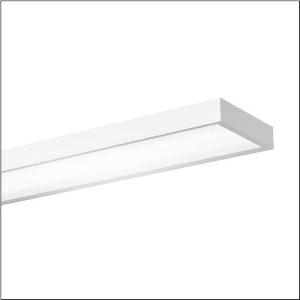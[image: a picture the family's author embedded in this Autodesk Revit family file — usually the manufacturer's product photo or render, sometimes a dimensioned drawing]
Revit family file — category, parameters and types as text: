
# Revit family: sport_31_51hs12dd4gca
name_source: partatom
category: Lighting Fixtures
units: mm (PartAtom-declared; Revit-internal decimal feet)

## family parameters
Cut with Voids When Loaded = No
Host = Face
Light Source = No
Part Type = Normal
Room Calculation Point = No
Round Connector Dimension = Use Diameter
Shared = No

## types (1)
- --- (1 x LED, 15290 lm, 113 W, 4000K)
    Apparent Load = 113 VA
    CIE Flux Codes = 65 89 97 100 100
    Color Rendering = 80
    Color Temperature = 4000K
    Default Elevation = 1800 mm
    Description = Sport 31, LED high bay luminaire, primary light control with reflector, of sheet steel, primary anti-glare with prismatic structure, of PC, primary optical cover: cover panel, of PC, light emission: direct distribution, primary light characteristic: symmetric, installation type: suspended mounting, recessed, surface-mounted, LED, rated luminous flux: 16.000lm, luminous efficacy: 137lm/W, light colour: 840, colour temperature: 4000K, control gear: ECG DALI, with terminal, 5-pole, max. 2.5mm², mains connection: 220..240V, AC/DC, 50/60Hz, rated input power: 117W, housing, of sheet steel, traffic white (RAL 9016), length: 1.540mm, width: 415mm, height: 95mm, protection rating (complete): IP20, protection rating (lamp compartment, on room side): IP50, insulation class (complete): insulation class I (protective earthing), certification: CE, ENEC, UKCA, ball protection: ball impact resistant with ceiling mounting or chain suspension, impact resistance: IK08, permissible operating ambient temperature: -20..+35°C, standard: DIN 18032-3, EN 60598-2-22, packaging unit: 1 piece
    Height = 100 mm  [stored 0.328084 ft]
    Lamp = 1 x LED
    Lamp Light Flux = 15290 lm
    Lamp Power = 113 W
    Lamp count = 1
    Length = 1500 mm
    Luminous efficacy = 135 lm/W
    Manufacturer = Siteco
    ModVariant = No
    Model = 51HS12DD4GCA
    Mounting Place = Ceiling
    Mounting Type = Pendant
    Number of Poles = 1
    OnlyDefault = Yes
    Power Factor = 1
    Product Name = Sport 31
    Product group = LED high bay luminaire
    ProductGroupID = 903
    Protection Class = Protection class I
    Protection Degree = IP 20
    RLX_Detail_Level = 1
    RLX_Emergency_Light_Flux = 0 lm
    RLX_Emergency_Type = 0
    RLX_Emergency_Type_DB = No
    RlxData = <blob elided: 24097 chars, md5=366df863>
    Socket = socket
    Standby Power = 0 W
    System Light Flux = 15290 lm
    System Power = 113 W
    Type Comments = factory setting: luminous flux: 100 % | dim-lin: 254 | 558 mA
    Type Image = l_1006829.jpg
    URL = http://relux.com
    VarID = @adj_133009
    Voltage = 0 V
    Weight = 0.00 kg
    Width = 415 mm

note: [stored X ft] marks values corroborated as IEEE doubles in the binary element streams (Revit-internal decimal feet)

## geometry (parser evidence)
native form markers: Blend x4, Sweep x9
no freeform markers — native parametric forms only
